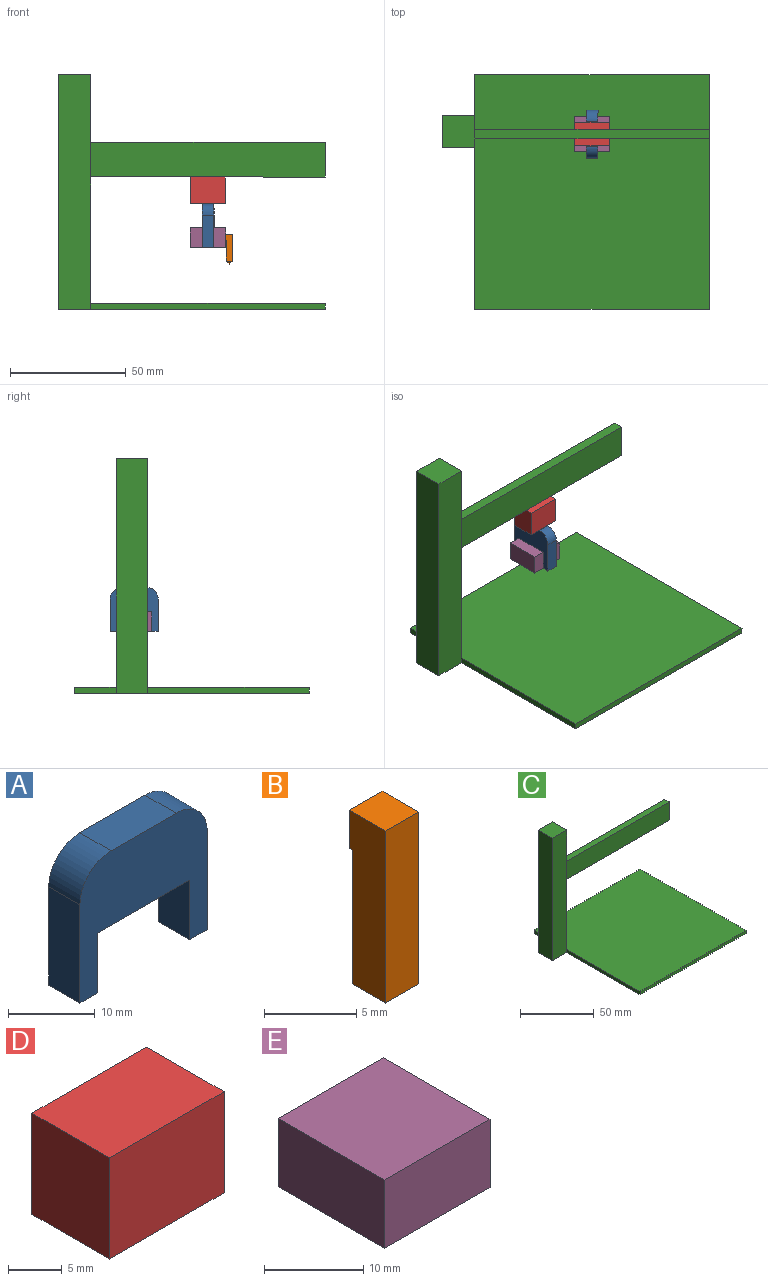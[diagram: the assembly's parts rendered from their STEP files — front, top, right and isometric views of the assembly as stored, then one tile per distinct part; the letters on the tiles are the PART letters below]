
ASSEMBLY  parts=5 mates=4
PART A: 12 faces, bbox 20.8x5.1x19 mm
  f0: plane 5.08x2.87mm, normal (0,0,-1), area 14.6mm2, adj f1,f7,f8,f9
  f1: plane 13.9x5.08mm, normal (1,0,0), area 70.6mm2, adj f0,f8,f9,f10
  f2: plane 10.61x5.08mm, normal (0,0,1), area 53.9mm2, adj f8,f9,f10,f11
  f3: plane 13.9x5.08mm, normal (-1,0,0), area 70.6mm2, adj f4,f8,f9,f11
  f4: plane 5.08x2.87mm, normal (0,0,-1), area 14.6mm2, adj f3,f5,f8,f9
  f5: plane 8.44x5.08mm, normal (1,0,0), area 42.9mm2, adj f4,f6,f8,f9
  f6: plane 15.03x5.08mm, normal (0,0,-1), area 76.4mm2, adj f5,f7,f8,f9
  f7: plane 8.44x5.08mm, normal (-1,0,0), area 42.9mm2, adj f0,f6,f8,f9
  f8: plane 20.77x18.98mm, normal (0,-1,0), area 256.5mm2, adj f0,f1,f2,f3,f4,f5,f6,f7
  f9: plane 20.77x18.98mm, normal (0,1,0), area 256.5mm2, adj f0,f1,f2,f3,f4,f5,f6,f7
  f10: cylinder r=5.08mm len=5.08mm, axis (0,1,0), area 40.5mm2, adj f1,f2,f8,f9
  f11: cylinder r=5.08mm len=5.08mm, axis (0,-1,0), area 40.5mm2, adj f2,f3,f8,f9
PART B: 11 faces, bbox 2.5x2.8x12.7 mm
  f0: plane 11.43x2.79mm, normal (1,0,0), area 29.7mm2, adj f1,f3,f4,f5,f6,f9
  f1: plane 2.79x2.54mm, normal (0,0,1), area 7.1mm2, adj f0,f2,f4,f5
  f2: plane 11.43x2.79mm, normal (-1,0,0), area 29.7mm2, adj f1,f3,f4,f5,f6,f8
  f3: plane 2.54x0.25mm, normal (0,0,-1), area 0.6mm2, adj f0,f2,f4,f6
  f4: plane 2.54x2.54mm, normal (0,1,0), area 6.5mm2, adj f0,f1,f2,f3
  f5: plane 11.43x2.54mm, normal (0,-1,0), area 29mm2, adj f0,f1,f2,f10
  f6: plane 8.89x2.54mm, normal (0,1,0), area 22.6mm2, adj f0,f2,f3,f7
  f7: plane 2.54x1.27mm, normal (0,0.71,-0.71), area 2.3mm2, adj f6,f8,f9
  f8: plane 2.54x1.27mm, normal (-0.71,0,-0.71), area 2.3mm2, adj f2,f7,f10
  f9: plane 2.54x1.27mm, normal (0.71,0,-0.71), area 2.3mm2, adj f0,f7,f10
  f10: plane 2.54x1.27mm, normal (0,-0.71,-0.71), area 2.3mm2, adj f5,f8,f9
PART C: 17 faces, bbox 115.5x101.6x101.6 mm
  f0: plane 99.06x13.57mm, normal (1,0,0), area 1282mm2, adj f6,f8,f10,f11,f12,f13,f14,f15
  f1: plane 70.09x2.54mm, normal (-1,0,0), area 178mm2, adj f3,f6,f7,f10
  f2: plane 17.94x2.54mm, normal (-1,0,0), area 45.6mm2, adj f5,f6,f7,f8
  f3: plane 101.6x2.54mm, normal (0,-1,0), area 258.1mm2, adj f1,f4,f6,f7
  f4: plane 101.6x2.54mm, normal (1,0,0), area 258.1mm2, adj f3,f5,f6,f7
  f5: plane 101.6x2.54mm, normal (0,1,0), area 258.1mm2, adj f2,f4,f6,f7
  f6: plane 101.6x101.6mm, normal (0,0,1), area 10322.6mm2, adj f0,f1,f2,f3,f4,f5
  f7: plane 115.47x101.6mm, normal (0,0,-1), area 10510.8mm2, adj f1,f2,f3,f4,f5,f8,f9,f10
  f8: plane 101.6x13.87mm, normal (0,1,0), area 1409.3mm2, adj f0,f2,f7,f9,f11
  f9: plane 101.6x13.57mm, normal (-1,0,0), area 1379mm2, adj f7,f8,f10,f11
  f10: plane 101.6x13.87mm, normal (0,-1,0), area 1409.3mm2, adj f0,f1,f7,f9,f11
  f11: plane 13.87x13.57mm, normal (0,0,1), area 188.3mm2, adj f0,f8,f9,f10
  f12: plane 101.6x15mm, normal (0,-1,0), area 1524.2mm2, adj f0,f13,f15,f16
  f13: plane 101.6x4.17mm, normal (0,0,-1), area 423.4mm2, adj f0,f12,f14,f16
  f14: plane 101.6x15mm, normal (0,1,0), area 1524.2mm2, adj f0,f13,f15,f16
  f15: plane 101.6x4.17mm, normal (0,0,1), area 423.4mm2, adj f0,f12,f14,f16
  f16: plane 15x4.17mm, normal (1,0,0), area 62.5mm2, adj f12,f13,f14,f15
PART D: 6 faces, bbox 15x10.2x11.5 mm
  f0: plane 11.48x10.16mm, normal (1,0,0), area 116.6mm2, adj f1,f3,f4,f5
  f1: plane 15.04x10.16mm, normal (0,0,1), area 152.8mm2, adj f0,f2,f4,f5
  f2: plane 11.48x10.16mm, normal (-1,0,0), area 116.6mm2, adj f1,f3,f4,f5
  f3: plane 15.04x10.16mm, normal (0,0,-1), area 152.8mm2, adj f0,f2,f4,f5
  f4: plane 15.04x11.48mm, normal (0,-1,0), area 172.6mm2, adj f0,f1,f2,f3
  f5: plane 15.04x11.48mm, normal (0,1,0), area 172.6mm2, adj f0,f1,f2,f3
PART E: 6 faces, bbox 15x15.2x8.4 mm
  f0: plane 15.24x8.44mm, normal (-1,0,0), area 128.6mm2, adj f1,f3,f4,f5
  f1: plane 15.24x15.03mm, normal (0,0,-1), area 229.1mm2, adj f0,f2,f4,f5
  f2: plane 15.24x8.44mm, normal (1,0,0), area 128.6mm2, adj f1,f3,f4,f5
  f3: plane 15.24x15.03mm, normal (0,0,1), area 229.1mm2, adj f0,f2,f4,f5
  f4: plane 15.03x8.44mm, normal (0,-1,0), area 126.8mm2, adj f0,f1,f2,f3
  f5: plane 15.03x8.44mm, normal (0,1,0), area 126.8mm2, adj f0,f1,f2,f3
PLACE A rot(axis=(0,0,1),89.7deg) t=(-34.62,24.85,-6.16)mm
PLACE B rot(axis=(0,0,1),89.7deg) t=(-34.62,24.81,-6.4)mm
PLACE C rot(axis=(0.8,0.6,-0.05),0deg) t=(-57.54,-0.05,-6.82)mm
PLACE D rot(axis=(0.8,0.6,-0.05),0deg) t=(-57.54,2.03,-6.39)mm
PLACE E rot(axis=(0,0,1),89.7deg) t=(-34.62,24.85,-6.16)mm
MATE revolute A.f2 <-> D.f3  axis (0,0,1) through (-57.53,24.94,39)mm
MATE fastened D.f1 <-> C.f13  axis (0,0,1) through (-57.52,24.93,50.48)mm
MATE fastened E.f3 <-> A.f6  axis (0,0,1) through (-57.53,24.94,28.45)mm
MATE revolute B.f4 <-> E.f4  axis (-1,0,0) through (-49.91,24.91,24.23)mm
